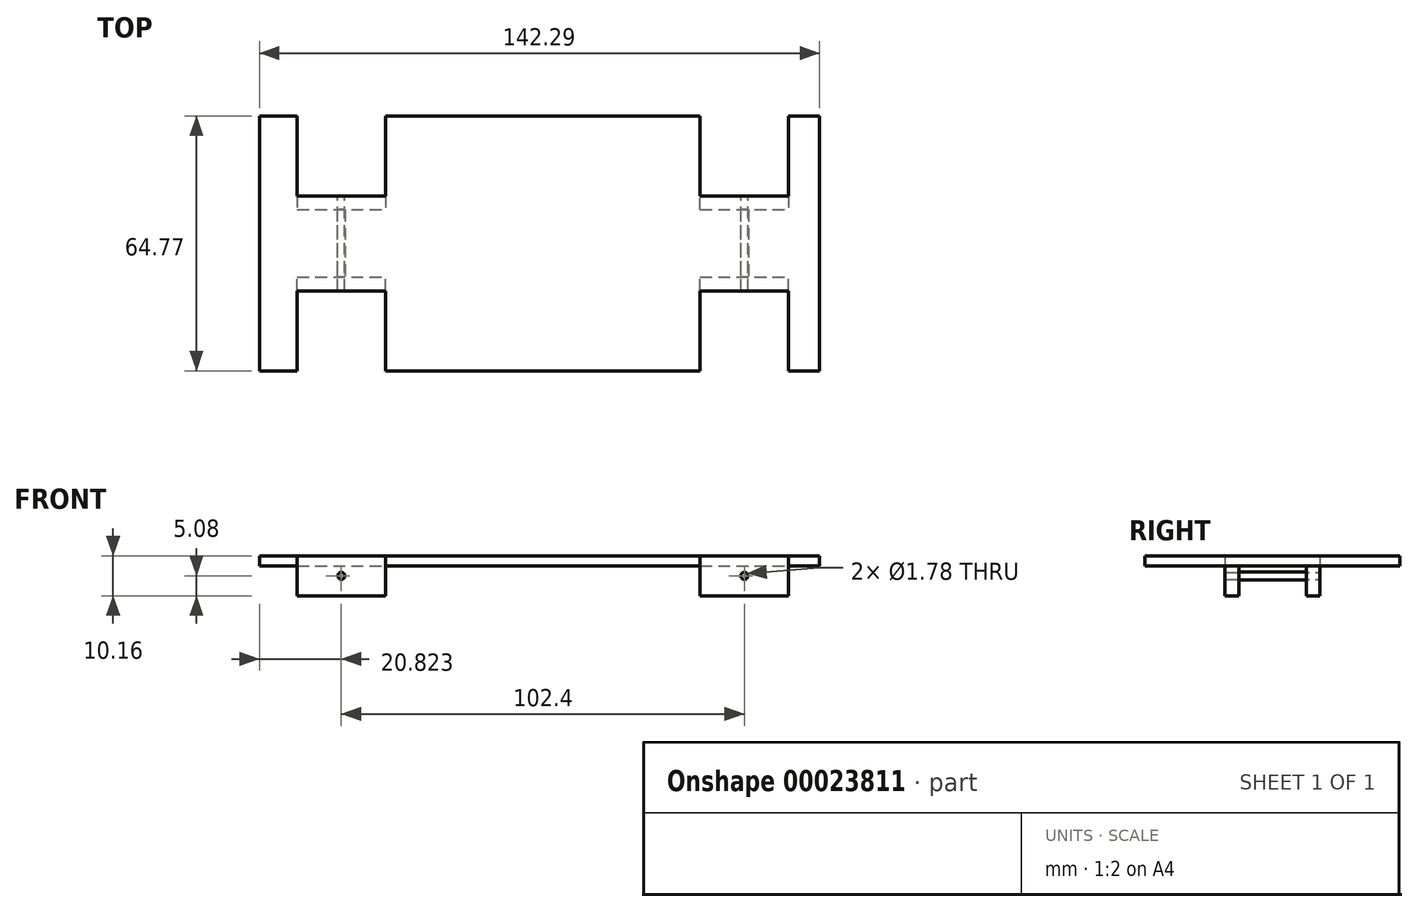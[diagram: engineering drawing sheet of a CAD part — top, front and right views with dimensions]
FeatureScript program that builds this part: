
annotation { "Feature Type Name" : "Feature", "Feature Type Description" : "" }
export const myFeature = defineFeature(function(context is Context, id is Id, definition is map)
    precondition{}
    {
        {
            var Q0;
            Q0=qCreatedBy(makeId("Top.planeOp"),FACE);
            var sketch = newSketch(context, id + "F0", { "sketchPlane" : qUnion([Q0])});
            skLineSegment(sketch, "E0.bottom", {"start": v(-72.06, 31.15) * mm, "end": v(70.23, 31.15) * mm});
            skLineSegment(sketch, "E0.top", {"start": v(-72.06, -33.62) * mm, "end": v(70.23, -33.62) * mm});
            skLineSegment(sketch, "E0.left", {"start": v(-72.06, 31.15) * mm, "end": v(-72.06, -33.62) * mm});
            skLineSegment(sketch, "E0.right", {"start": v(70.23, 31.15) * mm, "end": v(70.23, -33.62) * mm});
            skPoint(sketch, "E1", {"position": v(-62.45, 31.15) * mm});
            skPoint(sketch, "E2", {"position": v(-62.45, -33.62) * mm});
            skPoint(sketch, "E3", {"position": v(-40.02, 31.15) * mm});
            skPoint(sketch, "E4", {"position": v(-40.02, -33.62) * mm});
            skPoint(sketch, "E5", {"position": v(39.95, 31.15) * mm});
            skPoint(sketch, "E6", {"position": v(39.95, -33.62) * mm});
            skPoint(sketch, "E7", {"position": v(62.38, 31.15) * mm});
            skPoint(sketch, "E8", {"position": v(62.38, -33.62) * mm});
            skSolve(sketch);
        }
        {
            var Q0;
            Q0 = qSketchRegion(id + "F0", true);
            extrude(context, id + "F1", {"entities" : qUnion([Q0]), "depth" : 2.54 * mm});
        }
        {
            var Q0;
            Q0=makeQuery(id+"F0.imprint","IMPRINT",FACE,{"disambiguationData":[TD([[makeQuery(id+"F0.imprint","IMPRINT",EDGE,{"derivedFrom":sQuery(id+"F0.wireOp",EDGE,"E0.bottom")}),-1.0]])]});
            var sketch = newSketch(context, id + "F2", { "sketchPlane" : qUnion([Q0])});
            skLineSegment(sketch, "E9.bottom", {"start": v(-62.45, -33.62) * mm, "end": v(-40.02, -33.62) * mm});
            skLineSegment(sketch, "E9.top", {"start": v(-62.45, -13.3) * mm, "end": v(-40.02, -13.3) * mm});
            skLineSegment(sketch, "E9.left", {"start": v(-62.45, -33.62) * mm, "end": v(-62.45, -13.3) * mm});
            skLineSegment(sketch, "E9.right", {"start": v(-40.02, -33.62) * mm, "end": v(-40.02, -13.3) * mm});
            skLineSegment(sketch, "E10.bottom", {"start": v(-40.02, 31.15) * mm, "end": v(-62.45, 31.15) * mm});
            skLineSegment(sketch, "E10.top", {"start": v(-40.02, 10.83) * mm, "end": v(-62.45, 10.83) * mm});
            skLineSegment(sketch, "E10.left", {"start": v(-40.02, 31.15) * mm, "end": v(-40.02, 10.83) * mm});
            skLineSegment(sketch, "E10.right", {"start": v(-62.45, 31.15) * mm, "end": v(-62.45, 10.83) * mm});
            skLineSegment(sketch, "E11.bottom", {"start": v(62.38, -33.62) * mm, "end": v(39.95, -33.62) * mm});
            skLineSegment(sketch, "E11.top", {"start": v(62.38, -13.3) * mm, "end": v(39.95, -13.3) * mm});
            skLineSegment(sketch, "E11.left", {"start": v(62.38, -33.62) * mm, "end": v(62.38, -13.3) * mm});
            skLineSegment(sketch, "E11.right", {"start": v(39.95, -33.62) * mm, "end": v(39.95, -13.3) * mm});
            skLineSegment(sketch, "E12.bottom", {"start": v(62.38, 31.15) * mm, "end": v(39.95, 31.15) * mm});
            skLineSegment(sketch, "E12.top", {"start": v(62.38, 10.83) * mm, "end": v(39.95, 10.83) * mm});
            skLineSegment(sketch, "E12.left", {"start": v(62.38, 31.15) * mm, "end": v(62.38, 10.83) * mm});
            skLineSegment(sketch, "E12.right", {"start": v(39.95, 31.15) * mm, "end": v(39.95, 10.83) * mm});
            skSolve(sketch);
        }
        {
            var Q0;
            Q0 = qSketchRegion(id + "F2", true);
            extrude(context, id + "F3", {"entities" : qUnion([Q0]), "operationType" : NewBodyOperationType.REMOVE, "depth" : 25.4 * mm});
        }
        {
            var Q0;
            Q0=makeQuery(id+"F1.opExtrude","CAP_FACE",FACE,{"disambiguationData":[OSD([sQuery(id+"F0.wireOp",EDGE,"E0.bottom"),sQuery(id+"F0.wireOp",EDGE,"E0.top"),sQuery(id+"F0.wireOp",EDGE,"E0.left"),sQuery(id+"F0.wireOp",EDGE,"E0.right")])],"isStart":true});
            var sketch = newSketch(context, id + "F4", { "sketchPlane" : qUnion([Q0])});
            skLineSegment(sketch, "E13.bottom", {"start": v(-62.45, -10.83) * mm, "end": v(-40.02, -10.83) * mm});
            skLineSegment(sketch, "E13.top", {"start": v(-62.45, -7.33) * mm, "end": v(-40.02, -7.33) * mm});
            skLineSegment(sketch, "E13.left", {"start": v(-62.45, -10.83) * mm, "end": v(-62.45, -7.33) * mm});
            skLineSegment(sketch, "E13.right", {"start": v(-40.02, -10.83) * mm, "end": v(-40.02, -7.33) * mm});
            skLineSegment(sketch, "E14.bottom", {"start": v(-62.45, 13.3) * mm, "end": v(-40.02, 13.3) * mm});
            skLineSegment(sketch, "E14.top", {"start": v(-62.45, 9.8) * mm, "end": v(-40.02, 9.8) * mm});
            skLineSegment(sketch, "E14.left", {"start": v(-62.45, 13.3) * mm, "end": v(-62.45, 9.8) * mm});
            skLineSegment(sketch, "E14.right", {"start": v(-40.02, 13.3) * mm, "end": v(-40.02, 9.8) * mm});
            skLineSegment(sketch, "E15.left", {"start": v(39.95, 13.3) * mm, "end": v(39.95, 9.8) * mm});
            skLineSegment(sketch, "E15.top", {"start": v(39.95, 9.8) * mm, "end": v(62.38, 9.8) * mm});
            skLineSegment(sketch, "E15.bottom", {"start": v(39.95, 13.3) * mm, "end": v(62.38, 13.3) * mm});
            skLineSegment(sketch, "E15.right", {"start": v(62.38, 13.3) * mm, "end": v(62.38, 9.8) * mm});
            skLineSegment(sketch, "E16.left", {"start": v(39.95, -7.32) * mm, "end": v(39.95, -10.83) * mm});
            skLineSegment(sketch, "E16.top", {"start": v(39.95, -10.83) * mm, "end": v(62.38, -10.83) * mm});
            skLineSegment(sketch, "E16.bottom", {"start": v(39.95, -7.32) * mm, "end": v(62.38, -7.32) * mm});
            skLineSegment(sketch, "E17", {"start": v(62.38, -10.83) * mm, "end": v(62.38, -7.32) * mm});
            skSolve(sketch);
        }
        {
            var Q0;
            Q0 = qSketchRegion(id + "F4", true);
            extrude(context, id + "F5", {"entities" : qUnion([Q0]), "operationType" : NewBodyOperationType.ADD, "depth" : 7.62 * mm});
        }
        {
            var Q0;
            Q0=makeQuery(id+"F5.boolean.opBoolean","MERGE",FACE,{"derivedFrom":[makeQuery(id+"F3.boolean.opBoolean","COPY",FACE,{"derivedFrom":makeQuery(id+"F3.opExtrude","SWEPT_FACE",FACE,{"disambiguationData":[OSD([sQuery(id+"F2.wireOp",EDGE,"E9.top")])]})}),makeQuery(id+"F5.opExtrude","SWEPT_FACE",FACE,{"disambiguationData":[OSD([sQuery(id+"F4.wireOp",EDGE,"E14.bottom")])]})]});
            var sketch = newSketch(context, id + "F6", { "sketchPlane" : qUnion([Q0])});
            skCircle(sketch, "E18", {"center": v(-51.24, -2.54) * mm, "radius": 1.02 * mm});
            skPoint(sketch, "E18.centerSnap0", {"position": v(-51.24, 2.54) * mm});
            skCircle(sketch, "E19", {"center": v(51.16, -2.54) * mm, "radius": 1.02 * mm});
            skLineSegment(sketch, "E20", {"start": v(39.95, 2.54) * mm, "end": v(62.38, 2.54) * mm, "construction": true});
            skPoint(sketch, "E21", {"position": v(51.16, 2.54) * mm});
            skSolve(sketch);
        }
        {
            var Q0;
            Q0 = qSketchRegion(id + "F6", true);
            extrude(context, id + "F7", {"entities" : qUnion([Q0]), "operationType" : NewBodyOperationType.REMOVE, "endBound" : BoundingType.THROUGH_ALL, "oppositeDirection" : true, "depth" : 25.4 * mm});
        }
        {
            var Q0;
            Q0=makeQuery(id+"F5.opExtrude","SWEPT_FACE",FACE,{"disambiguationData":[OSD([sQuery(id+"F4.wireOp",EDGE,"E15.top")])]});
            var sketch = newSketch(context, id + "F8", { "sketchPlane" : qUnion([Q0])});
            skCircle(sketch, "E22", {"center": v(51.24, -2.54) * mm, "radius": 1.02 * mm});
            skCircle(sketch, "E23", {"center": v(-51.16, -2.54) * mm, "radius": 1.02 * mm});
            skSolve(sketch);
        }
        {
            var Q0;
            Q0 = qSketchRegion(id + "F8", true);
            extrude(context, id + "F9", {"entities" : qUnion([Q0]), "operationType" : NewBodyOperationType.ADD, "depth" : 20.62 * mm, "hasSecondDirection" : true, "secondDirectionOppositeDirection" : true, "secondDirectionDepth" : 3.5 * mm});
        }
        {
            var Q0;
            Q0=makeQuery(id+"F9.boolean.opBoolean","MERGE",FACE,{"derivedFrom":[makeQuery(id+"F5.boolean.opBoolean","MERGE",FACE,{"derivedFrom":[makeQuery(id+"F3.boolean.opBoolean","COPY",FACE,{"derivedFrom":makeQuery(id+"F3.opExtrude","SWEPT_FACE",FACE,{"disambiguationData":[OSD([sQuery(id+"F2.wireOp",EDGE,"E12.top")])]})}),makeQuery(id+"F5.opExtrude","SWEPT_FACE",FACE,{"disambiguationData":[OSD([sQuery(id+"F4.wireOp",EDGE,"E16.top")])]})]}),makeQuery(id+"F9.opExtrude","CAP_FACE",FACE,{"disambiguationData":[OSD([sQuery(id+"F8.wireOp",EDGE,"E23")])],"isStart":false})]});
            var sketch = newSketch(context, id + "F10", { "sketchPlane" : qUnion([Q0])});
            skCircle(sketch, "E24", {"center": v(-51.16, -2.54) * mm, "radius": 0.89 * mm});
            skPoint(sketch, "E24.centerSnap0", {"position": v(-51.16, 2.54) * mm});
            skCircle(sketch, "E25", {"center": v(51.24, -2.54) * mm, "radius": 0.89 * mm});
            skLineSegment(sketch, "E26", {"start": v(40.02, 2.54) * mm, "end": v(62.45, 2.54) * mm, "construction": true});
            skPoint(sketch, "E27", {"position": v(51.24, 2.54) * mm});
            skSolve(sketch);
        }
        {
            var Q0;
            Q0 = qSketchRegion(id + "F10", true);
            extrude(context, id + "F11", {"entities" : qUnion([Q0]), "operationType" : NewBodyOperationType.REMOVE, "endBound" : BoundingType.THROUGH_ALL, "oppositeDirection" : true, "depth" : 25.4 * mm});
        }
    });
